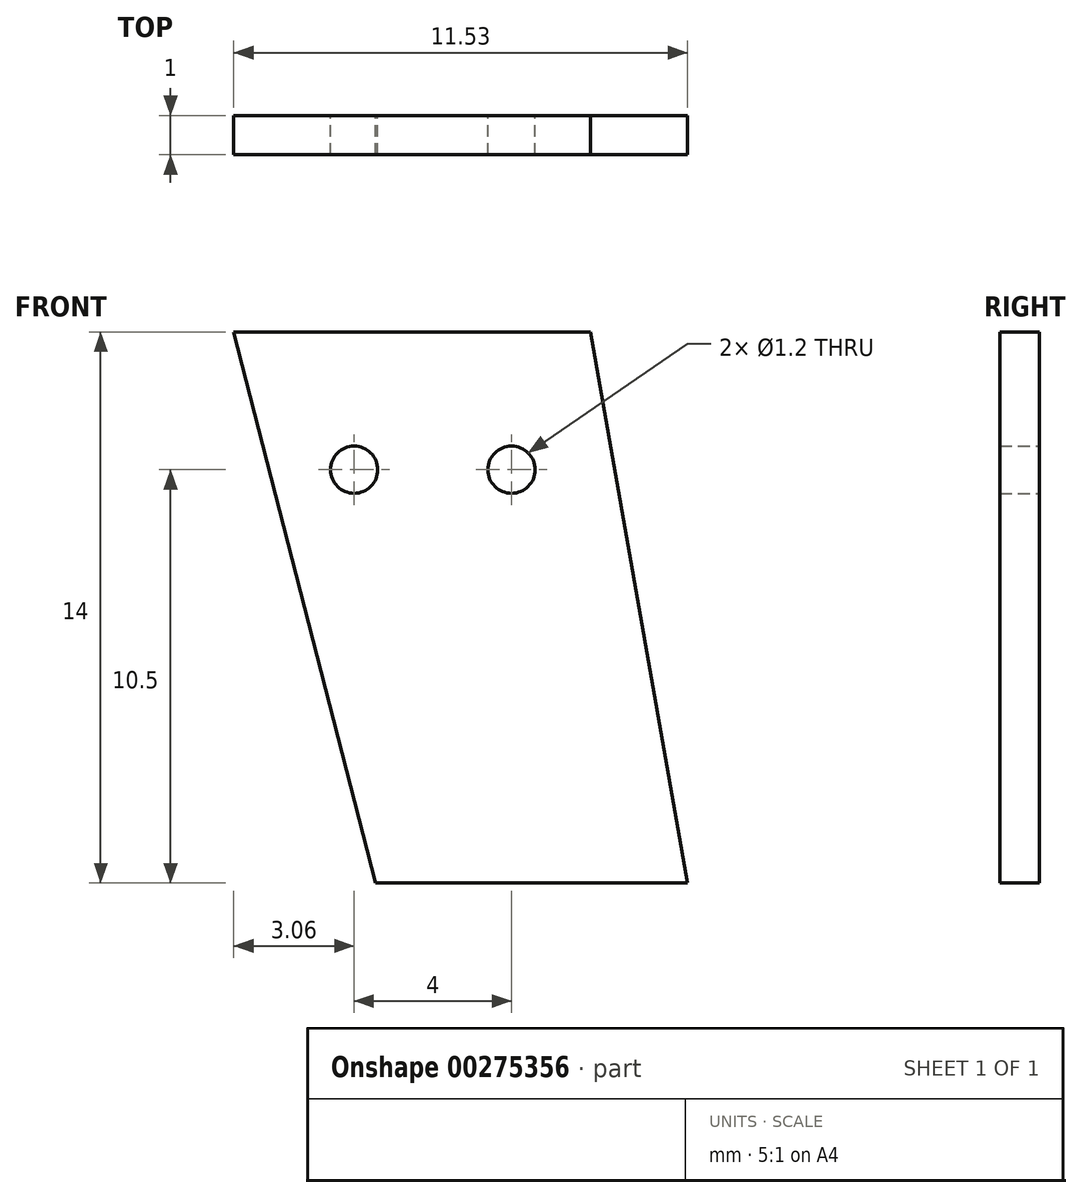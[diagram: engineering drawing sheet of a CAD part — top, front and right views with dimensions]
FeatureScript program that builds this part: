
annotation { "Feature Type Name" : "Feature", "Feature Type Description" : "" }
export const myFeature = defineFeature(function(context is Context, id is Id, definition is map)
    precondition{}
    {
        {
            assignVariable(context, id + "F0", {"name" : "ES", "anyValue" : 1});
        }
        {
            var Q0;
            Q0=qCreatedBy(makeId("Front.planeOp"),FACE);
            var sketch = newSketch(context, id + "F1", { "sketchPlane" : qUnion([Q0])});
            skLineSegment(sketch, "E0", {"start": v(25.52, 0) * mm, "end": v(27.99, -14) * mm});
            skLineSegment(sketch, "E1", {"start": v(34.34, -50) * mm, "end": v(29.34, -50) * mm, "construction": true});
            skLineSegment(sketch, "E2", {"start": v(20.06, -14) * mm, "end": v(18.52, -8) * mm});
            skLineSegment(sketch, "E3", {"start": v(18.52, -8) * mm, "end": v(16.46, -8) * mm, "construction": true});
            skLineSegment(sketch, "E4", {"start": v(25.52, 0) * mm, "end": v(16.46, 0) * mm});
            skCircle(sketch, "E5", {"center": v(19.52, -3.5) * mm, "radius": 0.6 * mm});
            skLineSegment(sketch, "E6", {"start": v(21.52, 0) * mm, "end": v(21.52, -8) * mm, "construction": true});
            skPoint(sketch, "E7", {"position": v(21.52, -3.5) * mm});
            skLineSegment(sketch, "E8", {"start": v(19.52, -3.5) * mm, "end": v(21.52, -3.5) * mm, "construction": true});
            skCircle(sketch, "E9.MirrorC", {"center": v(23.52, -3.5) * mm, "radius": 0.6 * mm});
            skLineSegment(sketch, "E10", {"start": v(20.06, -14) * mm, "end": v(27.99, -14) * mm});
            skLineSegment(sketch, "E11", {"start": v(20.06, -14) * mm, "end": v(29.34, -50) * mm, "construction": true});
            skLineSegment(sketch, "E12", {"start": v(27.99, -14) * mm, "end": v(34.34, -50) * mm, "construction": true});
            skLineSegment(sketch, "E13", {"start": v(0, 0) * mm, "end": v(16.46, 0) * mm, "construction": true});
            skLineSegment(sketch, "E14", {"start": v(16.46, -8) * mm, "end": v(0, -8) * mm, "construction": true});
            skLineSegment(sketch, "E15", {"start": v(0, -8) * mm, "end": v(0, 0) * mm, "construction": true});
            skLineSegment(sketch, "E16", {"start": v(18.52, -8) * mm, "end": v(16.46, 0) * mm});
            skSolve(sketch);
        }
        {
            var Q0;
            Q0=makeQuery(id+"F1.imprint","IMPRINT",FACE,{"disambiguationData":[TD([[makeQuery(id+"F1.imprint","IMPRINT",EDGE,{"derivedFrom":sQuery(id+"F1.wireOp",EDGE,"E0")}),-1.0]])]});
            extrude(context, id + "F2", {"entities" : qUnion([Q0]), "depth" : (getVariable(context, 'ES')) * mm, "offsetDistance" : 25 * mm});
        }
    });
